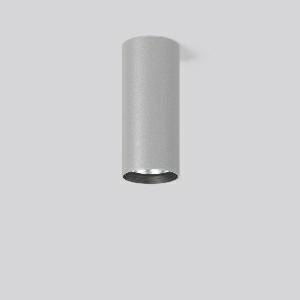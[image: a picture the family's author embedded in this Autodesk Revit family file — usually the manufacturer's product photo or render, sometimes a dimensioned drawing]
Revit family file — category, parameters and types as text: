
# Revit family: heledon_mini_a_931208_004_1_8ffe
name_source: partatom
category: Lighting Fixtures
units: mm (PartAtom-declared; Revit-internal decimal feet)

## family parameters
Cut with Voids When Loaded = No
Host = Face
Light Source = No
Part Type = Normal
Room Calculation Point = No
Round Connector Dimension = Use Diameter
Shared = No

## types (1)
- HELEDON mini A (1 x LED Modul 940, 3800 lm, 4000)
    Apparent Load = 29 VA
    Approval mark = CE
    CIE Flux Codes = 100 100 100 100 100
    Color Rendering = 92
    Color Temperature = 4000
    Default Elevation = 1800 mm
    Description = Series: HELEDON mini
Cylindrical surface-mounted downlight. Housing: die-cast aluminium, powder-coated. Internal ceiling frame polycarbonate with bayonet mounting. Black plastic ring and recessed LED to prevent glare from the side. Optical assembly with reflector made of MIRO-Silver with 98% total light reflection for outstanding efficiency - can be changed without tools. Best colour rendering index Ra>90. Suitable for Ceiling mounting. Easy installation with a separate ceiling frame with bayonet mounting and plug connection. Driver integrated. Connected via plug-in connector. High quality converter without flickering and stroboscopic effect. The following accessories can be mounted without use of tools: interchangeable lenses, decorative glasses, honeycomb louvre, clear and frosted diffusers, white interchangeable plastic ring. 
Colour: silver
Diameter: 87 mm
Height: 197 mm
Lamp: LED
Socket: without socket
Colour temperature: 4000K
Colour rendering index (CRI): 92
System power: 29 W
Rated luminous flux: 3800 lm
Luminous efficiency: 131 lm/W
Control gear: Regulated power supply
Protection class: I
Type of protection: IP 20
    Height = 197 mm
    Lamp = 1 x LED Modul 940
    Lamp Light Flux = 3800 lm
    Lamp count = 1
    Length = 87 mm
    Lifetime = 50000 h
    Luminous efficacy = 131 lm/W
    Manufacturer = RZB
    ModVariant = No
    Model = 931208.004.1
    Mounting Place = Ceiling
    Mounting Type = Surface mounted
    Number of Poles = 1
    OnlyDefault = Yes
    Power Factor = 1
    Product Name = HELEDON mini A
    Product group = Surface mounted downlights
    ProductGroupID = 302
    Protection Class = Protection class I
    Protection Degree = IP 20
    RLX_Detail_Level = 1
    RLX_Emergency_Light_Flux = 0 lm
    RLX_Emergency_Type = 0
    RLX_Emergency_Type_DB = No
    RlxData = <blob elided: 107421 chars, md5=ff83af67>
    Socket = socket
    Standby Power = 0 W
    System Light Flux = 3800 lm
    System Power = 29 W
    Type Comments = Product without accessories
    Type Image = 931188.004.jpg
    URL = http://relux.com
    VarID = ---
    Voltage = 230 V
    Voltage Range = 220-240 V
    Weight = 0.00 kg
    Width = 0 mm  [stored 0 ft]

note: [stored X ft] marks values corroborated as IEEE doubles in the binary element streams (Revit-internal decimal feet)

## geometry (parser evidence)
native form markers: Blend x4, Sweep x9
no freeform markers — native parametric forms only
